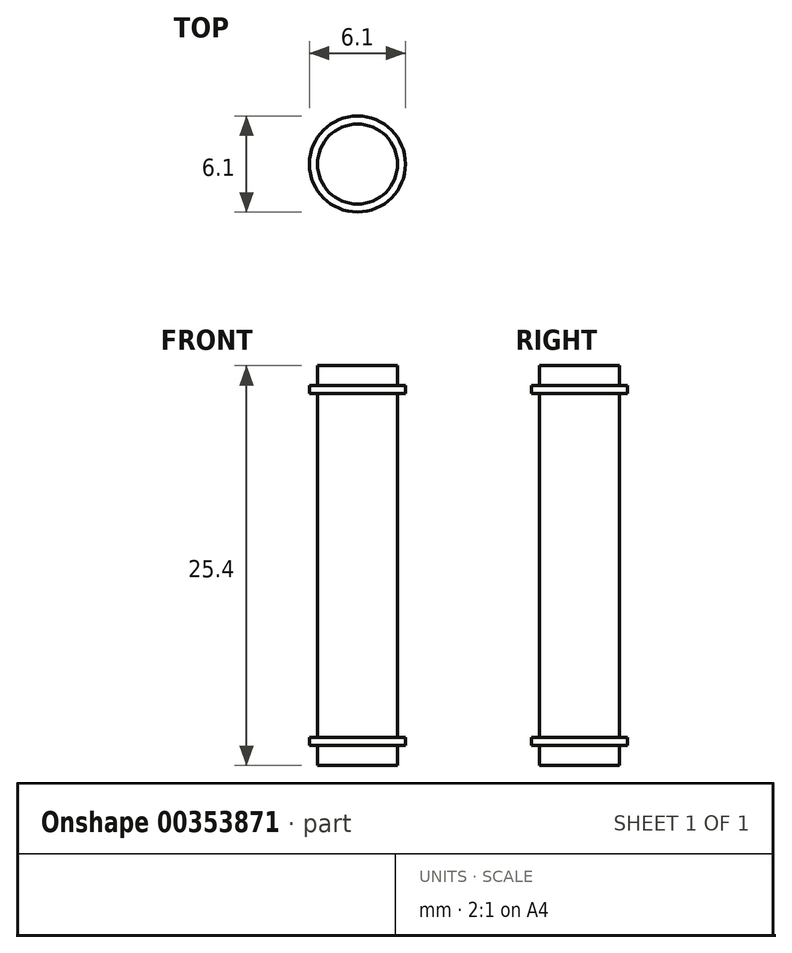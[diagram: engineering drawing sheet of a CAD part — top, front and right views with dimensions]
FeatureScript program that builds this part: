
annotation { "Feature Type Name" : "Feature", "Feature Type Description" : "" }
export const myFeature = defineFeature(function(context is Context, id is Id, definition is map)
    precondition{}
    {
        {
            var Q0;
            Q0=qCreatedBy(makeId("Top.planeOp"),FACE);
            var sketch = newSketch(context, id + "F0", { "sketchPlane" : qUnion([Q0])});
            skCircle(sketch, "E0", {"center": v(0, 0) * mm, "radius": 2.54 * mm});
            skSolve(sketch);
        }
        {
            var Q0;
            Q0 = qSketchRegion(id + "F0", true);
            extrude(context, id + "F1", {"entities" : qUnion([Q0]), "depth" : 25.4 * mm});
        }
        {
            var Q0;
            Q0=qCreatedBy(makeId("Top.planeOp"),FACE);
            cPlane(context, id + "F2", {"entities" : qUnion([Q0]), "cplaneType" : CPlaneType.OFFSET, "offset" : 1.78 * mm, "width" : 152.4 * mm, "height" : 152.4 * mm});
        }
        {
            var Q0;
            Q0=qCreatedBy(makeId("Top.planeOp"),FACE);
            cPlane(context, id + "F3", {"entities" : qUnion([Q0]), "cplaneType" : CPlaneType.OFFSET, "offset" : 23.62 * mm, "width" : 152.4 * mm, "height" : 152.4 * mm});
        }
        {
            var Q0;
            Q0=qCreatedBy(id+"F2.planeOp",FACE);
            var sketch = newSketch(context, id + "F4", { "sketchPlane" : qUnion([Q0])});
            skCircle(sketch, "E1", {"center": v(0, 0) * mm, "radius": 3.05 * mm});
            skSolve(sketch);
        }
        {
            var Q0;
            Q0=qCreatedBy(id+"F3.planeOp",FACE);
            var sketch = newSketch(context, id + "F5", { "sketchPlane" : qUnion([Q0])});
            skCircle(sketch, "E2", {"center": v(0, 0) * mm, "radius": 3.05 * mm});
            skSolve(sketch);
        }
        {
            var Q0;
            Q0=makeQuery(id+"F5.imprint","IMPRINT",FACE,{"disambiguationData":[TD([[makeQuery(id+"F5.imprint","IMPRINT",EDGE,{"derivedFrom":sQuery(id+"F5.wireOp",EDGE,"E2")}),1.0]])]});
            extrude(context, id + "F6", {"entities" : qUnion([Q0]), "operationType" : NewBodyOperationType.ADD, "depth" : 0.5 * mm});
        }
        {
            var Q0;
            Q0=makeQuery(id+"F4.imprint","IMPRINT",FACE,{"disambiguationData":[TD([[makeQuery(id+"F4.imprint","IMPRINT",EDGE,{"derivedFrom":sQuery(id+"F4.wireOp",EDGE,"E1")}),1.0]])]});
            extrude(context, id + "F7", {"entities" : qUnion([Q0]), "operationType" : NewBodyOperationType.ADD, "oppositeDirection" : true, "depth" : 0.5 * mm});
        }
    });
